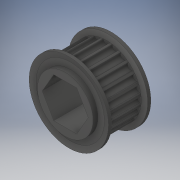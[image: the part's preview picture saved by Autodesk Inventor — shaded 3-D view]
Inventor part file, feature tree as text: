
AUTODESK INVENTOR PART (.ipt)
format: ipt  version: 2018 (Build 220112000, 112)  size: 313,344 bytes
history: native  units: in
note: dims shown in document units (in); Inventor stores cm internally (conversion verified against a paired STEP export)
features: mirror x1
ambient origin geometry x8: Origin, YZ Plane, XZ Plane, XY Plane, X Axis, Y Axis, Z Axis, Center Point
bodies: Solid1 (feature_tree)
feature tree (1):
  mirror  "Mirror1"
